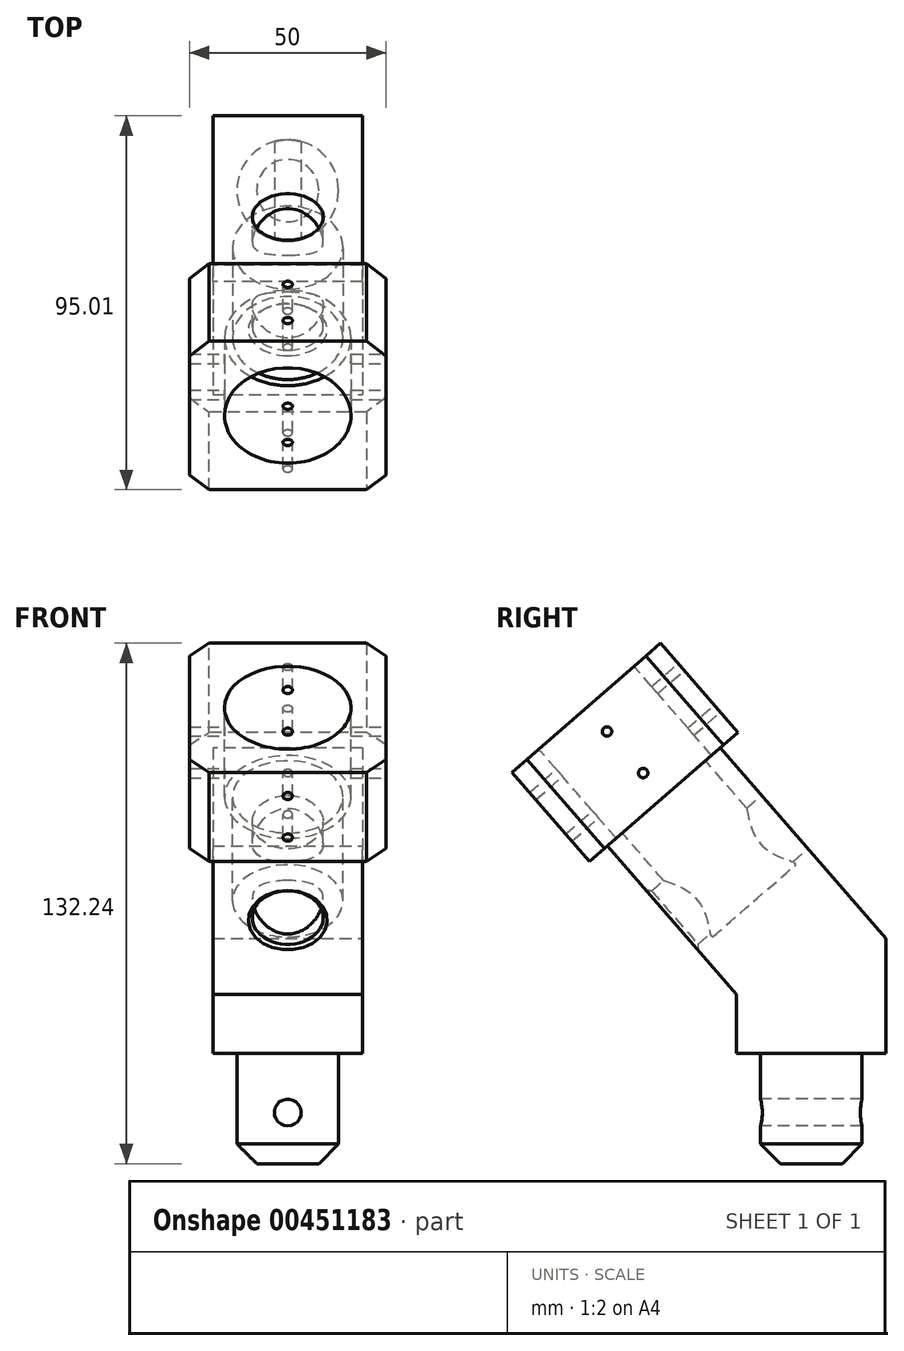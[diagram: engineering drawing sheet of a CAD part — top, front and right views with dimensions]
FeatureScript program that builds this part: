
annotation { "Feature Type Name" : "Feature", "Feature Type Description" : "" }
export const myFeature = defineFeature(function(context is Context, id is Id, definition is map)
    precondition{}
    {
        {
            var Q0;
            Q0=qCreatedBy(makeId("Top.planeOp"),FACE);
            var sketch = newSketch(context, id + "F0", { "sketchPlane" : qUnion([Q0])});
            skLineSegment(sketch, "E0.bottom", {"start": v(19, 19) * mm, "end": v(-19, 19) * mm});
            skLineSegment(sketch, "E0.top", {"start": v(19, -19) * mm, "end": v(-19, -19) * mm});
            skLineSegment(sketch, "E0.left", {"start": v(19, 19) * mm, "end": v(19, -19) * mm});
            skLineSegment(sketch, "E0.right", {"start": v(-19, 19) * mm, "end": v(-19, -19) * mm});
            skPoint(sketch, "E0.middle", {"position": v(0, 0) * mm});
            skSolve(sketch);
        }
        {
            var Q0;
            Q0 = qSketchRegion(id + "F0", true);
            extrude(context, id + "F1", {"entities" : qUnion([Q0]), "depth" : 15 * mm, "offsetDistance" : 25 * mm});
        }
        {
            var Q0;
            Q0=makeQuery(id+"F1.opExtrude","CAP_FACE",FACE,{"disambiguationData":[OSD([sQuery(id+"F0.wireOp",EDGE,"E0.bottom"),sQuery(id+"F0.wireOp",EDGE,"E0.top"),sQuery(id+"F0.wireOp",EDGE,"E0.left"),sQuery(id+"F0.wireOp",EDGE,"E0.right")])],"isStart":true});
            var sketch = newSketch(context, id + "F2", { "sketchPlane" : qUnion([Q0])});
            skCircle(sketch, "E1", {"center": v(0, 0) * mm, "radius": 12.9 * mm});
            skSolve(sketch);
        }
        {
            var Q0;
            Q0 = qSketchRegion(id + "F2", true);
            extrude(context, id + "F3", {"entities" : qUnion([Q0]), "operationType" : NewBodyOperationType.ADD, "depth" : 28 * mm, "offsetDistance" : 25 * mm});
        }
        {
            var Q0;
            Q0=qCreatedBy(makeId("Front.planeOp"),FACE);
            var sketch = newSketch(context, id + "F4", { "sketchPlane" : qUnion([Q0])});
            skCircle(sketch, "E2", {"center": v(0, -15) * mm, "radius": 3.4 * mm});
            skSolve(sketch);
        }
        {
            var Q0;
            Q0 = qSketchRegion(id + "F4", true);
            extrude(context, id + "F5", {"entities" : qUnion([Q0]), "operationType" : NewBodyOperationType.REMOVE, "oppositeDirection" : true, "depth" : 42 * mm, "offsetDistance" : 25 * mm, "symmetric" : true});
        }
        {
            var Q0;
            Q0=makeQuery(id+"F1.opExtrude","SWEPT_FACE",FACE,{"disambiguationData":[OSD([sQuery(id+"F0.wireOp",EDGE,"E0.left")])]});
            var sketch = newSketch(context, id + "F6", { "sketchPlane" : qUnion([Q0])});
            skLineSegment(sketch, "E3", {"start": v(-19, 15) * mm, "end": v(-71.48, 75.38) * mm});
            skLineSegment(sketch, "E4", {"start": v(-71.48, 75.38) * mm, "end": v(-42.8, 100.3) * mm});
            skLineSegment(sketch, "E5", {"start": v(19, 15) * mm, "end": v(-19, 15) * mm});
            skLineSegment(sketch, "E6", {"start": v(-42.8, 100.3) * mm, "end": v(19, 29.2) * mm});
            skLineSegment(sketch, "E7", {"start": v(19, 29.2) * mm, "end": v(19, 15) * mm});
            skLineSegment(sketch, "E8", {"start": v(-19, 15) * mm, "end": v(9.68, 39.93) * mm, "construction": true});
            skSolve(sketch);
        }
        {
            var Q0;
            Q0 = qSketchRegion(id + "F6", true);
            extrude(context, id + "F7", {"entities" : qUnion([Q0]), "operationType" : NewBodyOperationType.ADD, "oppositeDirection" : true, "depth" : 38 * mm, "offsetDistance" : 25 * mm});
        }
        {
            var Q0;
            Q0=makeQuery(id+"F7.opExtrude","SWEPT_FACE",FACE,{"disambiguationData":[OSD([sQuery(id+"F6.wireOp",EDGE,"E4")])]});
            var sketch = newSketch(context, id + "F8", { "sketchPlane" : qUnion([Q0])});
            skCircle(sketch, "E9", {"center": v(0, 14.5) * mm, "radius": 14 * mm});
            skSolve(sketch);
        }
        {
            var Q0;
            Q0 = qSketchRegion(id + "F8", true);
            extrude(context, id + "F9", {"entities" : qUnion([Q0]), "operationType" : NewBodyOperationType.REMOVE, "oppositeDirection" : true, "depth" : 65 * mm, "offsetDistance" : 25 * mm});
        }
        {
            var Q0;
            Q0=makeQuery(id+"F7.opExtrude","SWEPT_FACE",FACE,{"disambiguationData":[OSD([sQuery(id+"F6.wireOp",EDGE,"E4")])]});
            var sketch = newSketch(context, id + "F10", { "sketchPlane" : qUnion([Q0])});
            skCircle(sketch, "E10", {"center": v(0, 14.5) * mm, "radius": 16.05 * mm});
            skSolve(sketch);
        }
        {
            var Q0;
            Q0 = qSketchRegion(id + "F10", true);
            extrude(context, id + "F11", {"entities" : qUnion([Q0]), "operationType" : NewBodyOperationType.REMOVE, "oppositeDirection" : true, "depth" : 30 * mm, "offsetDistance" : 25 * mm});
        }
        {
            var Q0;
            Q0=makeQuery(id+"F7.opExtrude","SWEPT_FACE",FACE,{"disambiguationData":[OSD([sQuery(id+"F6.wireOp",EDGE,"E4")])]});
            var sketch = newSketch(context, id + "F12", { "sketchPlane" : qUnion([Q0])});
            skLineSegment(sketch, "E11.bottom", {"start": v(25, -10.5) * mm, "end": v(-25, -10.5) * mm});
            skLineSegment(sketch, "E11.top", {"start": v(25, 39.5) * mm, "end": v(-25, 39.5) * mm});
            skLineSegment(sketch, "E11.left", {"start": v(25, -10.5) * mm, "end": v(25, 39.5) * mm});
            skLineSegment(sketch, "E11.right", {"start": v(-25, -10.5) * mm, "end": v(-25, 39.5) * mm});
            skPoint(sketch, "E11.middle", {"position": v(0, 14.5) * mm});
            skCircle(sketch, "E12", {"center": v(0, 14.5) * mm, "radius": 16.05 * mm});
            skSolve(sketch);
        }
        {
            var Q0;
            Q0 = qSketchRegion(id + "F12", true);
            extrude(context, id + "F13", {"entities" : qUnion([Q0]), "operationType" : NewBodyOperationType.ADD, "oppositeDirection" : true, "depth" : 30 * mm, "offsetDistance" : 25 * mm});
        }
        {
            var Q0;
            Q0=makeQuery(id+"F7.opExtrude","SWEPT_FACE",FACE,{"disambiguationData":[OSD([sQuery(id+"F6.wireOp",EDGE,"E6")])]});
            var sketch = newSketch(context, id + "F14", { "sketchPlane" : qUnion([Q0])});
            skCircle(sketch, "E13", {"center": v(0, 48.79) * mm, "radius": 9 * mm});
            skSolve(sketch);
        }
        {
            var Q0;
            Q0 = qSketchRegion(id + "F14", true);
            extrude(context, id + "F15", {"entities" : qUnion([Q0]), "operationType" : NewBodyOperationType.REMOVE, "endBound" : BoundingType.THROUGH_ALL, "oppositeDirection" : true, "depth" : 25 * mm, "offsetDistance" : 25 * mm});
        }
        {
            var Q0;
            Q0=makeQuery(id+"F13.opExtrude","SWEPT_FACE",FACE,{"disambiguationData":[OSD([sQuery(id+"F12.wireOp",EDGE,"E11.top")])]});
            var sketch = newSketch(context, id + "F16", { "sketchPlane" : qUnion([Q0])});
            skCircle(sketch, "E14", {"center": v(0, 95.79) * mm, "radius": 1.2 * mm});
            skCircle(sketch, "E15", {"center": v(0, 81.79) * mm, "radius": 1.2 * mm});
            skSolve(sketch);
        }
        {
            var Q0;
            Q0 = qSketchRegion(id + "F16", true);
            extrude(context, id + "F17", {"entities" : qUnion([Q0]), "operationType" : NewBodyOperationType.REMOVE, "endBound" : BoundingType.THROUGH_ALL, "oppositeDirection" : true, "depth" : 25 * mm, "offsetDistance" : 25 * mm});
        }
        {
            var Q0;
            Q0=makeQuery(id+"F13.opExtrude","SWEPT_FACE",FACE,{"disambiguationData":[OSD([sQuery(id+"F12.wireOp",EDGE,"E11.left")])]});
            var sketch = newSketch(context, id + "F18", { "sketchPlane" : qUnion([Q0])});
            skCircle(sketch, "E16", {"center": v(-51.9, 81.8) * mm, "radius": 1.2 * mm});
            skCircle(sketch, "E17", {"center": v(-42.71, 71.24) * mm, "radius": 1.2 * mm});
            skSolve(sketch);
        }
        {
            var Q0;
            Q0 = qSketchRegion(id + "F18", true);
            extrude(context, id + "F19", {"entities" : qUnion([Q0]), "operationType" : NewBodyOperationType.REMOVE, "endBound" : BoundingType.THROUGH_ALL, "oppositeDirection" : true, "depth" : 25 * mm, "offsetDistance" : 25 * mm});
        }
        {
            var Q0;
            Q0=makeQuery(id+"F3.opExtrude","CAP_EDGE",EDGE,{"disambiguationData":[OSD([sQuery(id+"F2.wireOp",EDGE,"E1")])],"isStart":false});
            var Q1;
            Q1=makeQuery(id+"F13.opExtrude","SWEPT_EDGE",EDGE,{"disambiguationData":[OSD([sQuery(id+"F12.wireOp",EDGE,"E11.top"),sQuery(id+"F12.wireOp",EDGE,"E11.left")])]});
            var Q2;
            Q2=makeQuery(id+"F13.opExtrude","SWEPT_EDGE",EDGE,{"disambiguationData":[OSD([sQuery(id+"F12.wireOp",EDGE,"E11.bottom"),sQuery(id+"F12.wireOp",EDGE,"E11.left")])]});
            var Q3;
            Q3=makeQuery(id+"F13.opExtrude","SWEPT_EDGE",EDGE,{"disambiguationData":[OSD([sQuery(id+"F12.wireOp",EDGE,"E11.bottom"),sQuery(id+"F12.wireOp",EDGE,"E11.right")])]});
            var Q4;
            Q4=makeQuery(id+"F13.opExtrude","SWEPT_EDGE",EDGE,{"disambiguationData":[OSD([sQuery(id+"F12.wireOp",EDGE,"E11.top"),sQuery(id+"F12.wireOp",EDGE,"E11.right")])]});
            chamfer(context, id + "F20", {"entities" : qUnion([Q0, Q1, Q2, Q3, Q4]), "width" : 5 * mm, "tangentPropagation" : true});
        }
        {
            var Q0;
            Q0=makeQuery(id+"F11.boolean.opBoolean","COPY",EDGE,{"derivedFrom":makeQuery(id+"F11.opExtrude","CAP_EDGE",EDGE,{"disambiguationData":[OSD([sQuery(id+"F10.wireOp",EDGE,"E10")])],"isStart":true})});
            var Q1;
            Q1=makeQuery(id+"F15.boolean.opBoolean","INTERSECT",EDGE,{"derivedFrom":[makeQuery(id+"F7.opExtrude","SWEPT_FACE",FACE,{"disambiguationData":[OSD([sQuery(id+"F6.wireOp",EDGE,"E3")])]}),makeQuery(id+"F15.opExtrude","SWEPT_FACE",FACE,{"disambiguationData":[OSD([sQuery(id+"F14.wireOp",EDGE,"E13")])]})]});
            var Q2;
            Q2=makeQuery(id+"F15.boolean.opBoolean","COPY",EDGE,{"derivedFrom":makeQuery(id+"F15.opExtrude","CAP_EDGE",EDGE,{"disambiguationData":[OSD([sQuery(id+"F14.wireOp",EDGE,"E13")])],"isStart":true})});
            chamfer(context, id + "F21", {"entities" : qUnion([Q0, Q1, Q2]), "width" : 1 * mm, "tangentPropagation" : true});
        }
    });
